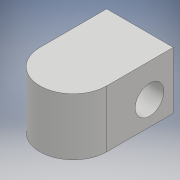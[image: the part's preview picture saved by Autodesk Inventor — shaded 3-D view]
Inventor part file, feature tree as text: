
AUTODESK INVENTOR PART (.ipt)
format: ipt  version: 2018.3 (Build 223284000, 284)  size: 117,248 bytes
history: native  units: mm
features: extrude x3, sketch x3, projected_geometry x1
ambient origin geometry x8: Origin, YZ Plane, XZ Plane, XY Plane, X Axis, Y Axis, Z Axis, Center Point
bodies: Solid1 (feature_tree)
feature tree (7):
  extrude  "Extrusion1"  Depth=3.0mm
  extrude  "Extrusion2"  Depth=10.0mm TaperAngle=0.0deg
  extrude  "Extrusion3"  Depth=2.0mm TaperAngle=0.0deg
  sketch  "Sketch1"  dims[d0=8.0mm d1=3.0mm]
  sketch  "Sketch2"  dims[d2=14.0mm d3=10.0mm d4=0.0mm]
  sketch  "Sketch3"  dims[d5=6.0mm d6=15.0mm d7=0.0mm d9=2.0mm d10=0.0mm]
  projected_geometry  "Projected Loop1"
